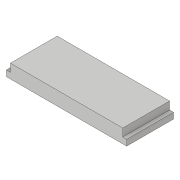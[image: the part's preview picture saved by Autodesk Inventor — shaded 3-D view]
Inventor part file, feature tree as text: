
AUTODESK INVENTOR PART (.ipt)
format: ipt  version: 2018.3 (Build 223284000, 284)  size: 89,088 bytes
history: native  units: in
note: dims shown in document units (in); Inventor stores cm internally (conversion verified against a paired STEP export)
features: extrude x2, sketch x2
ambient origin geometry x8: Origin, YZ Plane, XZ Plane, XY Plane, X Axis, Y Axis, Z Axis, Center Point
bodies: Solid1 (feature_tree)
feature tree (4):
  extrude  "Extrusion1"  Depth=0.75in
  extrude  "Extrusion5"  Depth=0.0625in
  sketch  "Sketch1"  dims[d0=1.925in d1=0.75in]
  sketch  "Sketch5"  dims[d2=0.22in d3=0.0in d17=0.0625in d18=0.0625in d19=0.125in d20=0.0in]
